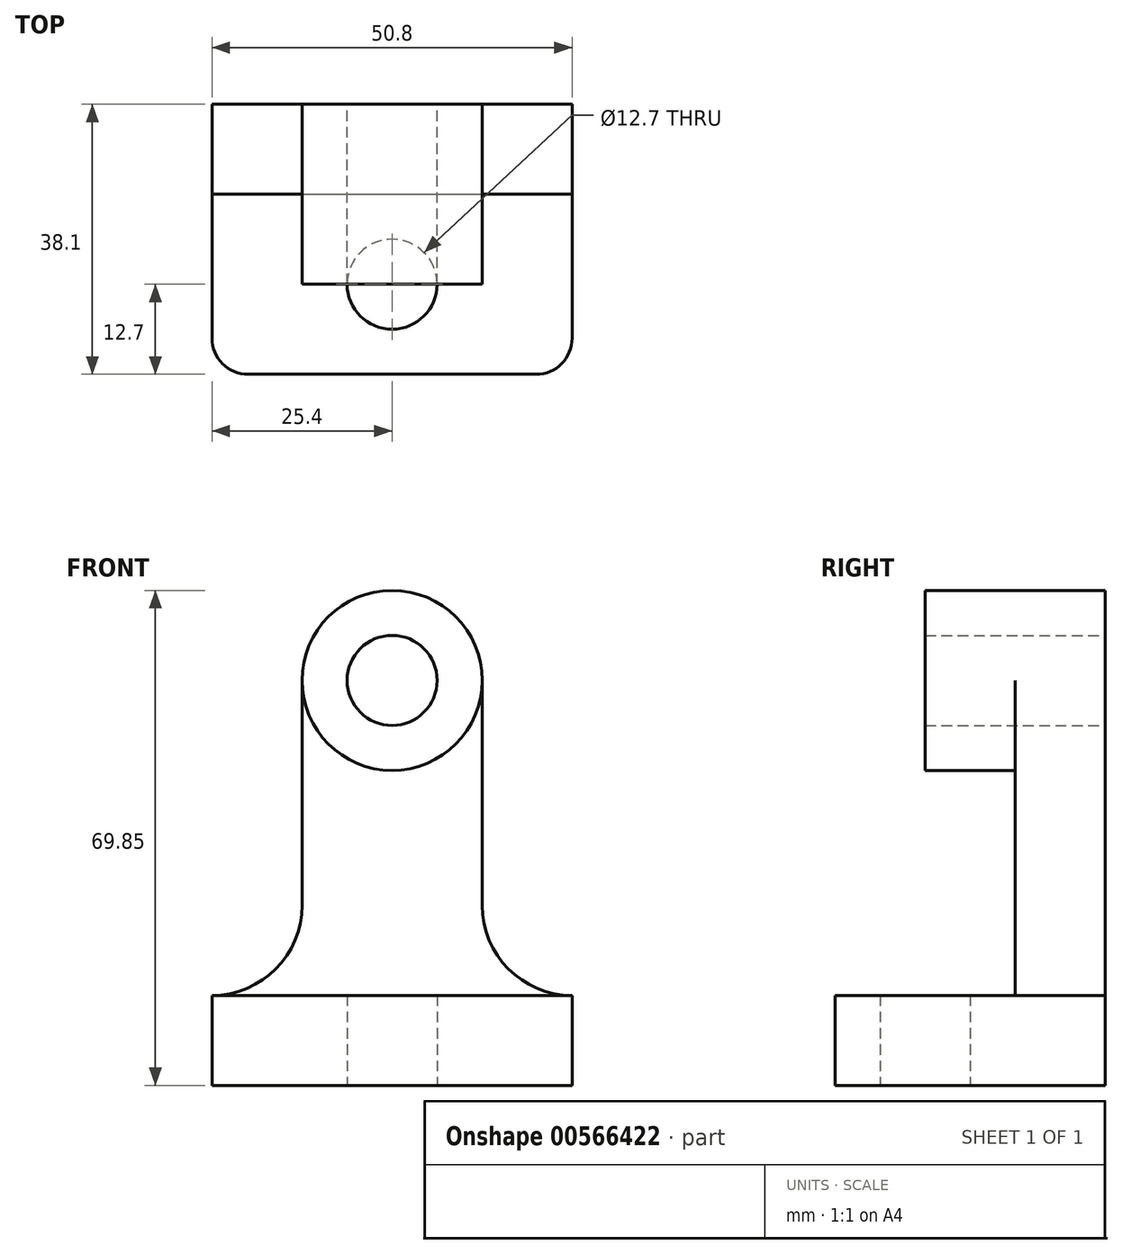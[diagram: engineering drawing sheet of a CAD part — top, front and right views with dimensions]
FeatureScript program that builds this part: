
annotation { "Feature Type Name" : "Feature", "Feature Type Description" : "" }
export const myFeature = defineFeature(function(context is Context, id is Id, definition is map)
    precondition{}
    {
        {
            var Q0;
            Q0=qCreatedBy(makeId("Front.planeOp"),FACE);
            var sketch = newSketch(context, id + "F0", { "sketchPlane" : qUnion([Q0])});
            skLineSegment(sketch, "E0", {"start": v(0, 0) * mm, "end": v(25.4, 0) * mm});
            skLineSegment(sketch, "E1", {"start": v(0, -12.7) * mm, "end": v(-25.4, -12.7) * mm});
            skLineSegment(sketch, "E2", {"start": v(-25.4, -12.7) * mm, "end": v(-25.4, 0) * mm});
            skLineSegment(sketch, "E3", {"start": v(-25.4, 0) * mm, "end": v(0, 0) * mm});
            skLineSegment(sketch, "E4", {"start": v(0, -12.7) * mm, "end": v(25.4, -12.7) * mm});
            skLineSegment(sketch, "E5", {"start": v(25.4, -12.7) * mm, "end": v(25.4, 0) * mm});
            skLineSegment(sketch, "E6", {"start": v(0, 0) * mm, "end": v(0, 57.15) * mm});
            skLineSegment(sketch, "E7", {"start": v(0, 0) * mm, "end": v(0, 44.45) * mm});
            skCircle(sketch, "E8", {"center": v(0, 44.45) * mm, "radius": 12.7 * mm});
            skLineSegment(sketch, "E9", {"start": v(0, 44.45) * mm, "end": v(12.7, 44.45) * mm});
            skLineSegment(sketch, "E10", {"start": v(12.7, 44.45) * mm, "end": v(12.7, 0) * mm});
            skLineSegment(sketch, "E11", {"start": v(0, 44.45) * mm, "end": v(-12.7, 44.45) * mm});
            skLineSegment(sketch, "E12", {"start": v(-12.7, 44.45) * mm, "end": v(-12.7, 0) * mm});
            skLineSegment(sketch, "E13.bottom", {"start": v(12.7, 0) * mm, "end": v(25.4, 0) * mm});
            skLineSegment(sketch, "E13.top", {"start": v(12.7, 12.7) * mm, "end": v(25.4, 12.7) * mm});
            skLineSegment(sketch, "E13.left", {"start": v(12.7, 0) * mm, "end": v(12.7, 12.7) * mm});
            skLineSegment(sketch, "E13.right", {"start": v(25.4, 0) * mm, "end": v(25.4, 12.7) * mm});
            skLineSegment(sketch, "E14.bottom", {"start": v(-12.7, 0) * mm, "end": v(-25.4, 0) * mm});
            skLineSegment(sketch, "E14.top", {"start": v(-12.7, 12.7) * mm, "end": v(-25.4, 12.7) * mm});
            skLineSegment(sketch, "E14.left", {"start": v(-12.7, 0) * mm, "end": v(-12.7, 12.7) * mm});
            skLineSegment(sketch, "E14.right", {"start": v(-25.4, 0) * mm, "end": v(-25.4, 12.7) * mm});
            skSolve(sketch);
        }
        {
            var Q0;
            Q0 = qSketchRegion(id + "F0", true);
            extrude(context, id + "F1", {"entities" : qUnion([Q0]), "depth" : 12.7 * mm, "offsetDistance" : 25.4 * mm});
        }
        {
            var Q0;
            Q0=makeQuery(id+"F1.opExtrude","CAP_FACE",FACE,{"disambiguationData":[OSD([sQuery(id+"F0.wireOp",EDGE,"E1"),sQuery(id+"F0.wireOp",EDGE,"E2"),sQuery(id+"F0.wireOp",EDGE,"E4"),sQuery(id+"F0.wireOp",EDGE,"E5"),sQuery(id+"F0.wireOp",EDGE,"E8"),sQuery(id+"F0.wireOp",EDGE,"E10"),sQuery(id+"F0.wireOp",EDGE,"E12"),sQuery(id+"F0.wireOp",EDGE,"E13.top"),sQuery(id+"F0.wireOp",EDGE,"E13.right"),sQuery(id+"F0.wireOp",EDGE,"E14.top"),sQuery(id+"F0.wireOp",EDGE,"E14.right")])],"isStart":true});
            var sketch = newSketch(context, id + "F2", { "sketchPlane" : qUnion([Q0])});
            skCircle(sketch, "E15", {"center": v(25.4, 12.7) * mm, "radius": 12.7 * mm});
            skCircle(sketch, "E16", {"center": v(-25.4, 12.7) * mm, "radius": 12.7 * mm});
            skSolve(sketch);
        }
        {
            var Q0;
            {var subQ1=makeQuery(id+"F1.opExtrude","CAP_EDGE",EDGE,{"disambiguationData":[OSD([sQuery(id+"F0.wireOp",EDGE,"E14.top")])],"isStart":true});Q0=makeQuery(id+"F2.imprint","IMPRINT",FACE,{"disambiguationData":[TD([[makeQuery(id+"F2.imprint","IMPRINT",EDGE,{"derivedFrom":subQ1}),-1.0]])]});}
            var Q1;
            {var subQ1=makeQuery(id+"F1.opExtrude","CAP_EDGE",EDGE,{"disambiguationData":[OSD([sQuery(id+"F0.wireOp",EDGE,"E13.top")])],"isStart":true});Q1=makeQuery(id+"F2.imprint","IMPRINT",FACE,{"disambiguationData":[TD([[makeQuery(id+"F2.imprint","IMPRINT",EDGE,{"derivedFrom":subQ1}),1.0]])]});}
            extrude(context, id + "F3", {"entities" : qUnion([Q0, Q1]), "operationType" : NewBodyOperationType.REMOVE, "oppositeDirection" : true, "depth" : 25.4 * mm, "offsetDistance" : 25.4 * mm});
        }
        {
            var Q0;
            Q0=makeQuery(id+"F1.opExtrude","CAP_FACE",FACE,{"disambiguationData":[OSD([sQuery(id+"F0.wireOp",EDGE,"E1"),sQuery(id+"F0.wireOp",EDGE,"E2"),sQuery(id+"F0.wireOp",EDGE,"E4"),sQuery(id+"F0.wireOp",EDGE,"E5"),sQuery(id+"F0.wireOp",EDGE,"E8"),sQuery(id+"F0.wireOp",EDGE,"E10"),sQuery(id+"F0.wireOp",EDGE,"E12"),sQuery(id+"F0.wireOp",EDGE,"E13.top"),sQuery(id+"F0.wireOp",EDGE,"E13.right"),sQuery(id+"F0.wireOp",EDGE,"E14.top"),sQuery(id+"F0.wireOp",EDGE,"E14.right")])],"isStart":false});
            var sketch = newSketch(context, id + "F4", { "sketchPlane" : qUnion([Q0])});
            skLineSegment(sketch, "E17.bottom", {"start": v(-25.4, -12.7) * mm, "end": v(25.4, -12.7) * mm});
            skLineSegment(sketch, "E17.top", {"start": v(-25.4, 0) * mm, "end": v(25.4, 0) * mm});
            skLineSegment(sketch, "E17.left", {"start": v(-25.4, -12.7) * mm, "end": v(-25.4, 0) * mm});
            skLineSegment(sketch, "E17.right", {"start": v(25.4, -12.7) * mm, "end": v(25.4, 0) * mm});
            skSolve(sketch);
        }
        {
            var Q0;
            Q0 = qSketchRegion(id + "F4", true);
            extrude(context, id + "F5", {"entities" : qUnion([Q0]), "operationType" : NewBodyOperationType.ADD, "depth" : 25.4 * mm, "offsetDistance" : 25.4 * mm});
        }
        {
            var Q0;
            Q0=makeQuery(id+"F5.opExtrude","CAP_EDGE",EDGE,{"disambiguationData":[OSD([sQuery(id+"F4.wireOp",EDGE,"E17.right")])],"isStart":false});
            var Q1;
            Q1=makeQuery(id+"F5.opExtrude","CAP_EDGE",EDGE,{"disambiguationData":[OSD([sQuery(id+"F4.wireOp",EDGE,"E17.left")])],"isStart":false});
            fillet(context, id + "F6", {"entities" : qUnion([Q0, Q1]), "radius" : 5.08 * mm, "tangentPropagation" : true, "allowEdgeOverflow" : false});
        }
        {
            var Q0;
            Q0=makeQuery(id+"F1.opExtrude","CAP_FACE",FACE,{"disambiguationData":[OSD([sQuery(id+"F0.wireOp",EDGE,"E1"),sQuery(id+"F0.wireOp",EDGE,"E2"),sQuery(id+"F0.wireOp",EDGE,"E4"),sQuery(id+"F0.wireOp",EDGE,"E5"),sQuery(id+"F0.wireOp",EDGE,"E8"),sQuery(id+"F0.wireOp",EDGE,"E10"),sQuery(id+"F0.wireOp",EDGE,"E12"),sQuery(id+"F0.wireOp",EDGE,"E13.top"),sQuery(id+"F0.wireOp",EDGE,"E13.right"),sQuery(id+"F0.wireOp",EDGE,"E14.top"),sQuery(id+"F0.wireOp",EDGE,"E14.right")])],"isStart":false});
            var sketch = newSketch(context, id + "F7", { "sketchPlane" : qUnion([Q0])});
            skCircle(sketch, "E18", {"center": v(0, 44.45) * mm, "radius": 12.7 * mm});
            skCircle(sketch, "E19", {"center": v(0, 44.45) * mm, "radius": 6.35 * mm});
            skSolve(sketch);
        }
        {
            var Q0;
            Q0 = qSketchRegion(id + "F7", true);
            extrude(context, id + "F8", {"entities" : qUnion([Q0]), "operationType" : NewBodyOperationType.ADD, "depth" : 12.7 * mm, "offsetDistance" : 25.4 * mm});
        }
        {
            var Q0;
            Q0=makeQuery(id+"F8.boolean.opBoolean","SPLIT",FACE,{"disambiguationData":[TD([makeQuery(id+"F8.opExtrude","SWEPT_FACE",FACE,{"disambiguationData":[OSD([sQuery(id+"F7.wireOp",EDGE,"E19")])]})])],"derivedFrom":makeQuery(id+"F1.opExtrude","CAP_FACE",FACE,{"disambiguationData":[OSD([sQuery(id+"F0.wireOp",EDGE,"E1"),sQuery(id+"F0.wireOp",EDGE,"E2"),sQuery(id+"F0.wireOp",EDGE,"E4"),sQuery(id+"F0.wireOp",EDGE,"E5"),sQuery(id+"F0.wireOp",EDGE,"E8"),sQuery(id+"F0.wireOp",EDGE,"E10"),sQuery(id+"F0.wireOp",EDGE,"E12"),sQuery(id+"F0.wireOp",EDGE,"E13.top"),sQuery(id+"F0.wireOp",EDGE,"E13.right"),sQuery(id+"F0.wireOp",EDGE,"E14.top"),sQuery(id+"F0.wireOp",EDGE,"E14.right")])],"isStart":false})});
            extrude(context, id + "F9", {"entities" : qUnion([Q0]), "operationType" : NewBodyOperationType.REMOVE, "oppositeDirection" : true, "depth" : 25.4 * mm, "offsetDistance" : 25.4 * mm});
        }
        {
            var Q0;
            Q0=makeQuery(id+"F5.boolean.opBoolean","MERGE",FACE,{"derivedFrom":[makeQuery(id+"F1.opExtrude","SWEPT_FACE",FACE,{"disambiguationData":[OSD([sQuery(id+"F0.wireOp",EDGE,"E1"),sQuery(id+"F0.wireOp",EDGE,"E4")])]}),makeQuery(id+"F5.opExtrude","SWEPT_FACE",FACE,{"disambiguationData":[OSD([sQuery(id+"F4.wireOp",EDGE,"E17.bottom")])]})]});
            var sketch = newSketch(context, id + "F10", { "sketchPlane" : qUnion([Q0])});
            skLineSegment(sketch, "E20", {"start": v(0, 0) * mm, "end": v(0, 38.1) * mm});
            skLineSegment(sketch, "E21", {"start": v(0, 38.1) * mm, "end": v(0, 25.4) * mm});
            skCircle(sketch, "E22", {"center": v(0, 25.4) * mm, "radius": 6.35 * mm});
            skSolve(sketch);
        }
        {
            var Q0;
            Q0 = qSketchRegion(id + "F10", true);
            extrude(context, id + "F11", {"entities" : qUnion([Q0]), "operationType" : NewBodyOperationType.REMOVE, "oppositeDirection" : true, "depth" : 25.4 * mm, "offsetDistance" : 25.4 * mm});
        }
    });
